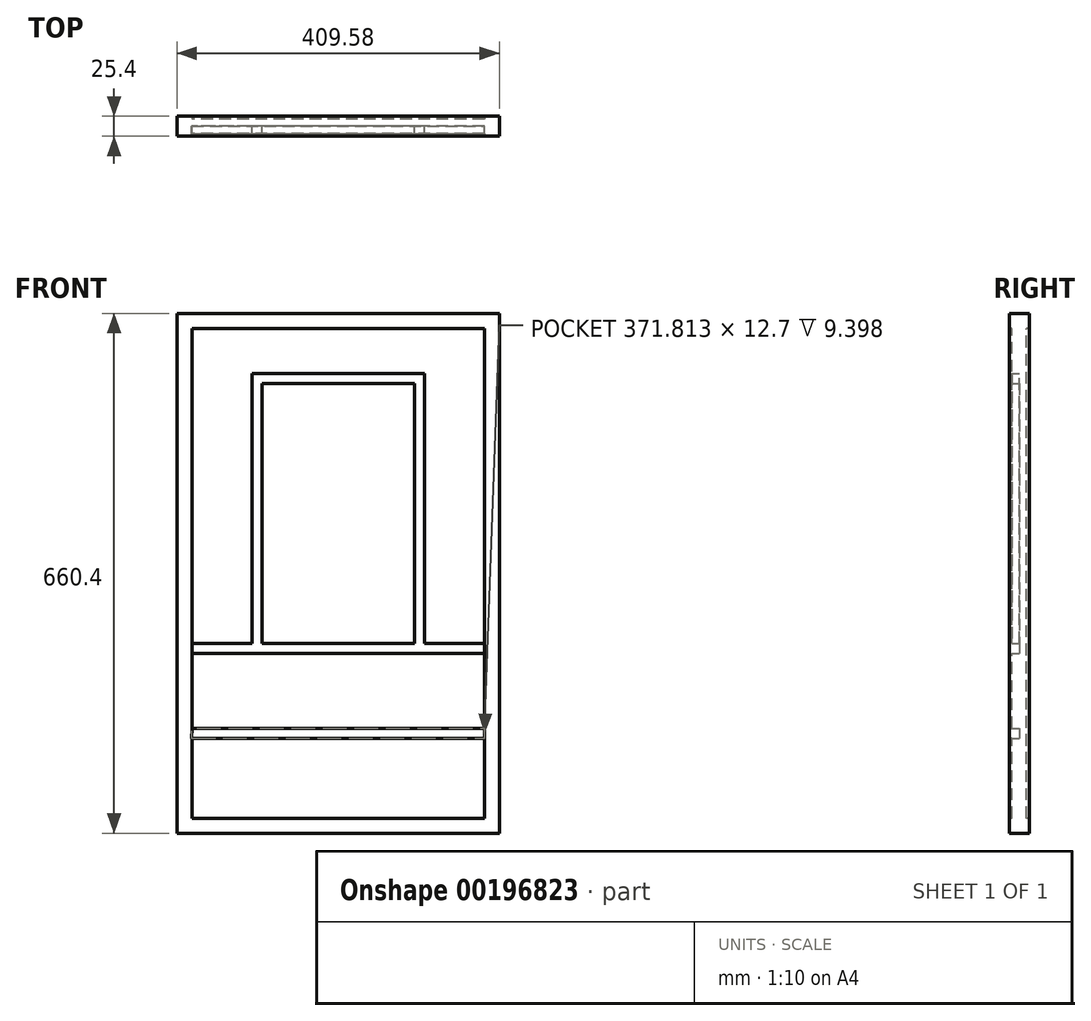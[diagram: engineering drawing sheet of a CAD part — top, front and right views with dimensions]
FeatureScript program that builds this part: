
annotation { "Feature Type Name" : "Feature", "Feature Type Description" : "" }
export const myFeature = defineFeature(function(context is Context, id is Id, definition is map)
    precondition{}
    {
        {
            var Q0;
            Q0=qCreatedBy(makeId("Front.planeOp"),FACE);
            var sketch = newSketch(context, id + "F0", { "sketchPlane" : qUnion([Q0])});
            skLineSegment(sketch, "E0.right", {"start": v(648.48, 526.34) * mm, "end": v(648.48, -95.96) * mm});
            skLineSegment(sketch, "E1.right", {"start": v(277, 526.34) * mm, "end": v(277, -95.96) * mm});
            skLineSegment(sketch, "E2.trimOffspring", {"start": v(277, 526.34) * mm, "end": v(648.48, 526.34) * mm});
            skPoint(sketch, "E0.left.start.orphan", {"position": v(-188.35, 507.3) * mm});
            skPoint(sketch, "E3.top.end.orphan", {"position": v(1132.45, -95.96) * mm});
            skLineSegment(sketch, "E4.top", {"start": v(257.95, -115) * mm, "end": v(667.53, -115) * mm});
            skLineSegment(sketch, "E4.left", {"start": v(257.95, 545.4) * mm, "end": v(257.95, -115) * mm});
            skLineSegment(sketch, "E4.right", {"start": v(667.53, 545.4) * mm, "end": v(667.53, -115) * mm});
            skLineSegment(sketch, "E5", {"start": v(257.95, 545.4) * mm, "end": v(667.53, 545.4) * mm});
            skLineSegment(sketch, "E6", {"start": v(648.48, -95.96) * mm, "end": v(277, -95.96) * mm});
            skLineSegment(sketch, "E7", {"start": v(667.53, 545.4) * mm, "end": v(648.48, 526.34) * mm});
            skLineSegment(sketch, "E8", {"start": v(257.95, 545.4) * mm, "end": v(277, 526.34) * mm});
            skLineSegment(sketch, "E9", {"start": v(257.95, -115) * mm, "end": v(277, -95.96) * mm});
            skLineSegment(sketch, "E10", {"start": v(648.48, -95.96) * mm, "end": v(667.53, -115) * mm});
            skSolve(sketch);
        }
        {
            var Q0;
            Q0=makeQuery(id+"F0.imprint","IMPRINT",FACE,{"disambiguationData":[TD([[makeQuery(id+"F0.imprint","IMPRINT",EDGE,{"derivedFrom":sQuery(id+"F0.wireOp",EDGE,"E0.bottom")}),-1.0]])]});
            var Q1;
            {var subQ0=sQuery(id+"F0.wireOp",EDGE,"E0.left");Q1=makeQuery(id+"F0.imprint","IMPRINT",FACE,{"disambiguationData":[TD([[makeQuery(id+"F0.imprint","IMPRINT",EDGE,{"derivedFrom":subQ0}),1.0]])]});}
            var Q2;
            Q2=makeQuery(id+"F0.imprint","IMPRINT",FACE,{"disambiguationData":[TD([[makeQuery(id+"F0.imprint","IMPRINT",EDGE,{"derivedFrom":sQuery(id+"F0.wireOp",EDGE,"E3.bottom")}),-1.0]])]});
            var Q3;
            Q3=makeQuery(id+"F0.imprint","IMPRINT",FACE,{"disambiguationData":[TD([[makeQuery(id+"F0.imprint","IMPRINT",EDGE,{"derivedFrom":sQuery(id+"F0.wireOp",EDGE,"E2.trimOffspring")}),1.0]])]});
            var Q4;
            Q4=makeQuery(id+"F0.imprint","IMPRINT",FACE,{"disambiguationData":[TD([[makeQuery(id+"F0.imprint","IMPRINT",EDGE,{"derivedFrom":sQuery(id+"F0.wireOp",EDGE,"E1.right")}),-1.0]])]});
            var Q5;
            Q5=makeQuery(id+"F0.imprint","IMPRINT",FACE,{"disambiguationData":[TD([[makeQuery(id+"F0.imprint","IMPRINT",EDGE,{"derivedFrom":sQuery(id+"F0.wireOp",EDGE,"E0.right")}),1.0]])]});
            var Q6;
            Q6=makeQuery(id+"F0.imprint","IMPRINT",FACE,{"disambiguationData":[TD([[makeQuery(id+"F0.imprint","IMPRINT",EDGE,{"derivedFrom":sQuery(id+"F0.wireOp",EDGE,"E4.top")}),1.0]])]});
            extrude(context, id + "F1", {"entities" : qUnion([Q0, Q1, Q2, Q3, Q4, Q5, Q6]), "oppositeDirection" : true, "depth" : 12.7 * mm, "hasSecondDirection" : true, "secondDirectionOppositeDirection" : true, "secondDirectionDepth" : -12.7 * mm, "offsetDistance" : 25.4 * mm});
        }
        {
            var Q0;
            Q0=qSketchRegion(id+"F0",true);
            var Q1;
            Q1=makeQuery(id+"F0.imprint","IMPRINT",FACE,{"disambiguationData":[TD([[makeQuery(id+"F0.imprint","IMPRINT",EDGE,{"derivedFrom":sQuery(id+"F0.wireOp",EDGE,"E0.right")}),-1.0]])]});
            extrude(context, id + "F2", {"entities" : qUnion([Q0, Q1]), "operationType" : NewBodyOperationType.ADD, "depth" : 9.4 * mm, "offsetDistance" : 25.4 * mm, "hasSecondDirection" : true, "secondDirectionOppositeDirection" : false, "secondDirectionDepth" : -9.4 * mm});
        }
        {
            var Q0;
            Q0=makeQuery(id+"F0.imprint","IMPRINT",FACE,{"disambiguationData":[TD([[makeQuery(id+"F0.imprint","IMPRINT",EDGE,{"derivedFrom":sQuery(id+"F0.wireOp",EDGE,"E0.right")}),-1.0]])]});
            var sketch = newSketch(context, id + "F3", { "sketchPlane" : qUnion([Q0])});
            skLineSegment(sketch, "E11.bottom", {"start": v(648.48, 5.64) * mm, "end": v(276.67, 5.64) * mm});
            skLineSegment(sketch, "E11.right", {"start": v(276.67, 5.64) * mm, "end": v(277, 18.34) * mm});
            skLineSegment(sketch, "E12", {"start": v(648.48, 18.34) * mm, "end": v(648.48, 5.64) * mm});
            skLineSegment(sketch, "E13.top", {"start": v(572.28, 469.2) * mm, "end": v(353.2, 469.2) * mm});
            skLineSegment(sketch, "E14.trimOffspring", {"start": v(559.58, 456.5) * mm, "end": v(365.9, 456.5) * mm});
            skLineSegment(sketch, "E15.bottom", {"start": v(648.48, 126.3) * mm, "end": v(572.28, 126.3) * mm});
            skLineSegment(sketch, "E15.left", {"start": v(648.48, 126.3) * mm, "end": v(648.48, 113.6) * mm});
            skLineSegment(sketch, "E15.right", {"start": v(277, 126.3) * mm, "end": v(277, 113.6) * mm});
            skLineSegment(sketch, "E16.trimOffspring", {"start": v(559.58, 126.3) * mm, "end": v(365.9, 126.3) * mm});
            skLineSegment(sketch, "E17", {"start": v(572.28, 456.5) * mm, "end": v(572.28, 469.2) * mm});
            skLineSegment(sketch, "E18", {"start": v(559.58, 456.5) * mm, "end": v(559.58, 126.3) * mm});
            skLineSegment(sketch, "E19", {"start": v(572.28, 126.3) * mm, "end": v(572.28, 469.2) * mm});
            skLineSegment(sketch, "E20", {"start": v(353.2, 126.3) * mm, "end": v(353.2, 456.5) * mm});
            skLineSegment(sketch, "E21", {"start": v(365.9, 126.3) * mm, "end": v(365.9, 456.5) * mm});
            skLineSegment(sketch, "E22", {"start": v(353.2, 469.2) * mm, "end": v(353.2, 456.5) * mm});
            skLineSegment(sketch, "E23.trimOffspring", {"start": v(353.2, 126.3) * mm, "end": v(277, 126.3) * mm});
            skLineSegment(sketch, "E24", {"start": v(277, 113.6) * mm, "end": v(648.48, 113.6) * mm});
            skLineSegment(sketch, "E25", {"start": v(277, 18.34) * mm, "end": v(648.48, 18.34) * mm});
            skSolve(sketch);
        }
        {
            var Q0;
            Q0=qSketchRegion(id+"F3",true);
            extrude(context, id + "F4", {"entities" : qUnion([Q0]), "operationType" : NewBodyOperationType.REMOVE, "depth" : 12.7 * mm, "offsetDistance" : 25.4 * mm});
        }
    });
